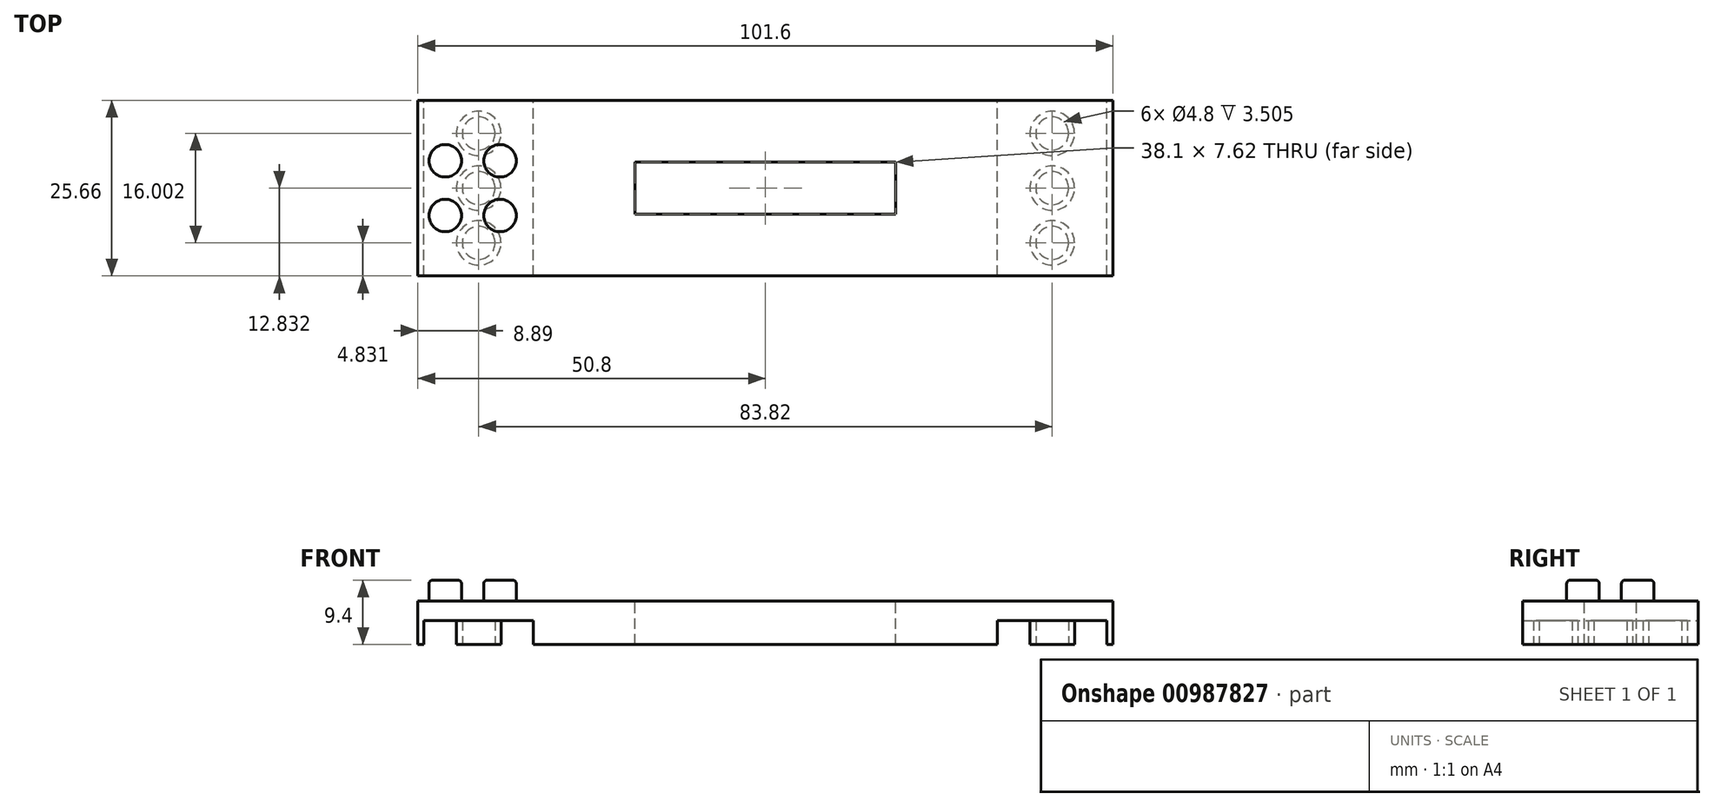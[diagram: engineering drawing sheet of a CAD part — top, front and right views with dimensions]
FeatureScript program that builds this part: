
annotation { "Feature Type Name" : "Feature", "Feature Type Description" : "" }
export const myFeature = defineFeature(function(context is Context, id is Id, definition is map)
    precondition{}
    {
        {
            var Q0;
            Q0=qCreatedBy(makeId("Top.planeOp"),FACE);
            var sketch = newSketch(context, id + "F0", { "sketchPlane" : qUnion([Q0])});
            skLineSegment(sketch, "E0.bottom", {"start": v(0, 0) * mm, "end": v(101.6, 0) * mm});
            skLineSegment(sketch, "E0.top", {"start": v(0, 32) * mm, "end": v(101.6, 32) * mm});
            skLineSegment(sketch, "E0.left", {"start": v(0, 0) * mm, "end": v(0, 32) * mm});
            skLineSegment(sketch, "E0.right", {"start": v(101.6, 0) * mm, "end": v(101.6, 32) * mm});
            skSolve(sketch);
        }
        {
            var Q0;
            Q0=makeQuery(id+"F0.imprint","IMPRINT",FACE,{"disambiguationData":[TD([[makeQuery(id+"F0.imprint","IMPRINT",EDGE,{"derivedFrom":sQuery(id+"F0.wireOp",EDGE,"E0.bottom")}),1.0]])]});
            extrude(context, id + "F1", {"entities" : qUnion([Q0]), "depth" : 6.35 * mm, "offsetDistance" : 25.4 * mm});
        }
        {
            var Q0;
            Q0=makeQuery(id+"F1.opExtrude","CAP_FACE",FACE,{"disambiguationData":[OSD([sQuery(id+"F0.wireOp",EDGE,"E0.bottom"),sQuery(id+"F0.wireOp",EDGE,"E0.top"),sQuery(id+"F0.wireOp",EDGE,"E0.left"),sQuery(id+"F0.wireOp",EDGE,"E0.right")])],"isStart":false});
            var sketch = newSketch(context, id + "F2", { "sketchPlane" : qUnion([Q0])});
            skCircle(sketch, "E1", {"center": v(4, 20) * mm, "radius": 2.37 * mm});
            skCircle(sketch, "E2.0.1.0", {"center": v(4, 12) * mm, "radius": 2.37 * mm});
            skCircle(sketch, "E2.1.0.0", {"center": v(12, 20) * mm, "radius": 2.37 * mm});
            skCircle(sketch, "E2.1.1.0", {"center": v(12, 12) * mm, "radius": 2.37 * mm});
            skLineSegment(sketch, "E2.direction1", {"start": v(4, 20) * mm, "end": v(12, 20) * mm, "construction": true});
            skLineSegment(sketch, "E2.direction2", {"start": v(4, 20) * mm, "end": v(4, 12) * mm, "construction": true});
            skLineSegment(sketch, "E3", {"start": v(4, 20) * mm, "end": v(4, 12) * mm});
            skLineSegment(sketch, "E4", {"start": v(12, 20) * mm, "end": v(12, 12) * mm, "construction": true});
            skLineSegment(sketch, "E5", {"start": v(4, 16) * mm, "end": v(12, 16) * mm, "construction": true});
            skSolve(sketch);
        }
        {
            var Q0;
            Q0=makeQuery(id+"F2.imprint","IMPRINT",FACE,{"disambiguationData":[TD([[makeQuery(id+"F2.imprint","IMPRINT",EDGE,{"derivedFrom":sQuery(id+"F2.wireOp",EDGE,"E2.1.0.0")}),1.0]])]});
            var Q1;
            Q1=makeQuery(id+"F2.imprint","IMPRINT",FACE,{"disambiguationData":[TD([[makeQuery(id+"F2.imprint","IMPRINT",EDGE,{"derivedFrom":sQuery(id+"F2.wireOp",EDGE,"E2.1.1.0")}),1.0]])]});
            var Q2;
            Q2=makeQuery(id+"F2.imprint","IMPRINT",FACE,{"disambiguationData":[TD([[makeQuery(id+"F2.imprint","IMPRINT",EDGE,{"derivedFrom":sQuery(id+"F2.wireOp",EDGE,"E2.0.1.0")}),1.0]])]});
            var Q3;
            Q3=makeQuery(id+"F2.imprint","IMPRINT",FACE,{"disambiguationData":[TD([[makeQuery(id+"F2.imprint","IMPRINT",EDGE,{"derivedFrom":sQuery(id+"F2.wireOp",EDGE,"E1")}),1.0]])]});
            extrude(context, id + "F3", {"entities" : qUnion([Q0, Q1, Q2, Q3]), "operationType" : NewBodyOperationType.ADD, "depth" : 3.05 * mm, "offsetDistance" : 25.4 * mm});
        }
        {
            var Q0;
            Q0=makeQuery(id+"F3.opExtrude","CAP_EDGE",EDGE,{"disambiguationData":[OSD([sQuery(id+"F2.wireOp",EDGE,"E2.1.0.0")])],"isStart":false});
            var Q1;
            Q1=makeQuery(id+"F3.opExtrude","CAP_EDGE",EDGE,{"disambiguationData":[OSD([sQuery(id+"F2.wireOp",EDGE,"E1")])],"isStart":false});
            var Q2;
            Q2=makeQuery(id+"F3.opExtrude","CAP_EDGE",EDGE,{"disambiguationData":[OSD([sQuery(id+"F2.wireOp",EDGE,"E2.0.1.0")])],"isStart":false});
            var Q3;
            Q3=makeQuery(id+"F3.opExtrude","CAP_EDGE",EDGE,{"disambiguationData":[OSD([sQuery(id+"F2.wireOp",EDGE,"E2.1.1.0")])],"isStart":false});
            fillet(context, id + "F4", {"entities" : qUnion([Q0, Q1, Q2, Q3]), "radius" : 0.5 * mm, "tangentPropagation" : true, "allowEdgeOverflow" : false});
        }
        {
            var Q0;
            Q0=makeQuery(id+"F1.opExtrude","CAP_FACE",FACE,{"disambiguationData":[OSD([sQuery(id+"F0.wireOp",EDGE,"E0.bottom"),sQuery(id+"F0.wireOp",EDGE,"E0.top"),sQuery(id+"F0.wireOp",EDGE,"E0.left"),sQuery(id+"F0.wireOp",EDGE,"E0.right")])],"isStart":true});
            var sketch = newSketch(context, id + "F5", { "sketchPlane" : qUnion([Q0])});
            skLineSegment(sketch, "E6.bottom", {"start": v(0, -32) * mm, "end": v(17.78, -32) * mm, "construction": true});
            skLineSegment(sketch, "E6.top", {"start": v(0, 0) * mm, "end": v(17.78, 0) * mm, "construction": true});
            skLineSegment(sketch, "E6.left", {"start": v(0, -32) * mm, "end": v(0, 0) * mm, "construction": true});
            skLineSegment(sketch, "E6.right", {"start": v(17.78, -32) * mm, "end": v(17.78, 0) * mm, "construction": true});
            skLineSegment(sketch, "E7.bottom", {"start": v(101.6, 0) * mm, "end": v(83.82, 0) * mm, "construction": true});
            skLineSegment(sketch, "E7.top", {"start": v(101.6, -32) * mm, "end": v(83.82, -32) * mm, "construction": true});
            skLineSegment(sketch, "E7.left", {"start": v(101.6, 0) * mm, "end": v(101.6, -32) * mm, "construction": true});
            skLineSegment(sketch, "E7.right", {"start": v(83.82, 0) * mm, "end": v(83.82, -32) * mm, "construction": true});
            skCircle(sketch, "E8", {"center": v(8.9, -16) * mm, "radius": 3.25 * mm});
            skCircle(sketch, "E9", {"center": v(8.9, -16) * mm, "radius": 2.4 * mm});
            skCircle(sketch, "E10", {"center": v(8.9, -8) * mm, "radius": 3.25 * mm});
            skCircle(sketch, "E11", {"center": v(8.9, -8) * mm, "radius": 2.4 * mm});
            skCircle(sketch, "E12", {"center": v(8.9, -24) * mm, "radius": 3.25 * mm});
            skCircle(sketch, "E13", {"center": v(8.9, -24) * mm, "radius": 2.4 * mm});
            skCircle(sketch, "E14", {"center": v(92.71, -16) * mm, "radius": 3.25 * mm});
            skCircle(sketch, "E15", {"center": v(92.71, -16) * mm, "radius": 2.4 * mm});
            skCircle(sketch, "E16", {"center": v(92.71, -8) * mm, "radius": 3.25 * mm});
            skCircle(sketch, "E17", {"center": v(92.71, -8) * mm, "radius": 2.4 * mm});
            skCircle(sketch, "E18", {"center": v(92.71, -24) * mm, "radius": 3.25 * mm});
            skCircle(sketch, "E19", {"center": v(92.71, -24) * mm, "radius": 2.4 * mm});
            skLineSegment(sketch, "E20", {"start": v(0, -16) * mm, "end": v(8.9, -16) * mm, "construction": true});
            skLineSegment(sketch, "E21", {"start": v(101.6, -16) * mm, "end": v(92.71, -16) * mm, "construction": true});
            skLineSegment(sketch, "E22", {"start": v(8.9, 0) * mm, "end": v(8.9, -8) * mm, "construction": true});
            skLineSegment(sketch, "E23", {"start": v(92.71, 0) * mm, "end": v(92.71, -8) * mm, "construction": true});
            skLineSegment(sketch, "E24", {"start": v(8.9, -8) * mm, "end": v(8.9, -16) * mm, "construction": true});
            skLineSegment(sketch, "E25", {"start": v(8.9, -16) * mm, "end": v(8.9, -24) * mm, "construction": true});
            skLineSegment(sketch, "E26", {"start": v(92.71, -8) * mm, "end": v(92.71, -16) * mm, "construction": true});
            skLineSegment(sketch, "E27", {"start": v(92.71, -16) * mm, "end": v(92.71, -24) * mm, "construction": true});
            skLineSegment(sketch, "E28.bottom", {"start": v(0.89, -1.5) * mm, "end": v(16.9, -1.5) * mm});
            skLineSegment(sketch, "E28.top", {"start": v(0.89, -30.5) * mm, "end": v(16.9, -30.5) * mm});
            skLineSegment(sketch, "E28.left", {"start": v(0.89, -1.5) * mm, "end": v(0.89, -30.5) * mm});
            skLineSegment(sketch, "E28.right", {"start": v(16.9, -1.5) * mm, "end": v(16.9, -30.5) * mm});
            skLineSegment(sketch, "E29.bottom", {"start": v(84.7, -1.5) * mm, "end": v(100.71, -1.5) * mm});
            skLineSegment(sketch, "E29.top", {"start": v(84.7, -30.5) * mm, "end": v(100.71, -30.5) * mm});
            skLineSegment(sketch, "E29.left", {"start": v(84.7, -1.5) * mm, "end": v(84.7, -30.5) * mm});
            skLineSegment(sketch, "E29.right", {"start": v(100.71, -1.5) * mm, "end": v(100.71, -30.5) * mm});
            skSolve(sketch);
        }
        {
            var Q0;
            Q0=makeQuery(id+"F5.imprint","IMPRINT",FACE,{"disambiguationData":[TD([[makeQuery(id+"F5.imprint","IMPRINT",EDGE,{"derivedFrom":sQuery(id+"F5.wireOp",EDGE,"E8")}),-1.0]])]});
            var Q1;
            Q1=makeQuery(id+"F5.imprint","IMPRINT",FACE,{"disambiguationData":[TD([[makeQuery(id+"F5.imprint","IMPRINT",EDGE,{"derivedFrom":sQuery(id+"F5.wireOp",EDGE,"E14")}),-1.0]])]});
            var Q2;
            Q2=makeQuery(id+"F5.imprint","IMPRINT",FACE,{"disambiguationData":[TD([[makeQuery(id+"F5.imprint","IMPRINT",EDGE,{"derivedFrom":sQuery(id+"F5.wireOp",EDGE,"E11")}),1.0]])]});
            var Q3;
            Q3=makeQuery(id+"F5.imprint","IMPRINT",FACE,{"disambiguationData":[TD([[makeQuery(id+"F5.imprint","IMPRINT",EDGE,{"derivedFrom":sQuery(id+"F5.wireOp",EDGE,"E9")}),1.0]])]});
            var Q4;
            Q4=makeQuery(id+"F5.imprint","IMPRINT",FACE,{"disambiguationData":[TD([[makeQuery(id+"F5.imprint","IMPRINT",EDGE,{"derivedFrom":sQuery(id+"F5.wireOp",EDGE,"E13")}),1.0]])]});
            var Q5;
            Q5=makeQuery(id+"F5.imprint","IMPRINT",FACE,{"disambiguationData":[TD([[makeQuery(id+"F5.imprint","IMPRINT",EDGE,{"derivedFrom":sQuery(id+"F5.wireOp",EDGE,"E17")}),1.0]])]});
            var Q6;
            Q6=makeQuery(id+"F5.imprint","IMPRINT",FACE,{"disambiguationData":[TD([[makeQuery(id+"F5.imprint","IMPRINT",EDGE,{"derivedFrom":sQuery(id+"F5.wireOp",EDGE,"E15")}),1.0]])]});
            var Q7;
            Q7=makeQuery(id+"F5.imprint","IMPRINT",FACE,{"disambiguationData":[TD([[makeQuery(id+"F5.imprint","IMPRINT",EDGE,{"derivedFrom":sQuery(id+"F5.wireOp",EDGE,"E19")}),1.0]])]});
            extrude(context, id + "F6", {"entities" : qUnion([Q0, Q1, Q2, Q3, Q4, Q5, Q6, Q7]), "operationType" : NewBodyOperationType.REMOVE, "oppositeDirection" : true, "depth" : 3.5 * mm, "offsetDistance" : 25.4 * mm});
        }
        {
            var Q0;
            {var subQ0=sQuery(id+"F0.wireOp",EDGE,"E0.bottom");var subQ1=sQuery(id+"F0.wireOp",EDGE,"E0.right");var subQ2=sQuery(id+"F0.wireOp",EDGE,"E0.top");var subQ3=sQuery(id+"F0.wireOp",EDGE,"E0.left");Q0=makeQuery(id+"F6.boolean.opBoolean","SPLIT",FACE,{"disambiguationData":[TD([makeQuery(id+"F1.opExtrude","SWEPT_FACE",FACE,{"disambiguationData":[OSD([subQ0])]})])],"derivedFrom":makeQuery(id+"F1.opExtrude","CAP_FACE",FACE,{"disambiguationData":[OSD([subQ0,subQ2,subQ3,subQ1])],"isStart":true})});}
            var sketch = newSketch(context, id + "F7", { "sketchPlane" : qUnion([Q0])});
            skLineSegment(sketch, "E30.bottom", {"start": v(101.6, -32) * mm, "end": v(0, -32) * mm});
            skLineSegment(sketch, "E30.top", {"start": v(101.6, -28.83) * mm, "end": v(0, -28.83) * mm});
            skLineSegment(sketch, "E30.left", {"start": v(101.6, -32) * mm, "end": v(101.6, -28.83) * mm});
            skLineSegment(sketch, "E30.right", {"start": v(0, -32) * mm, "end": v(0, -28.83) * mm});
            skLineSegment(sketch, "E31.bottom", {"start": v(101.6, 0) * mm, "end": v(0, 0) * mm});
            skLineSegment(sketch, "E31.top", {"start": v(101.6, -3.17) * mm, "end": v(0, -3.18) * mm});
            skLineSegment(sketch, "E31.left", {"start": v(101.6, 0) * mm, "end": v(101.6, -3.17) * mm});
            skLineSegment(sketch, "E31.right", {"start": v(0, 0) * mm, "end": v(0, -3.18) * mm});
            skSolve(sketch);
        }
        {
            var Q0;
            Q0 = qSketchRegion(id + "F7", true);
            extrude(context, id + "F8", {"entities" : qUnion([Q0]), "operationType" : NewBodyOperationType.REMOVE, "endBound" : BoundingType.UP_TO_NEXT, "oppositeDirection" : true, "depth" : 25.4 * mm, "offsetDistance" : 25.4 * mm});
        }
        {
            var Q0;
            Q0=makeQuery(id+"F1.opExtrude","CAP_FACE",FACE,{"disambiguationData":[OSD([sQuery(id+"F0.wireOp",EDGE,"E0.bottom"),sQuery(id+"F0.wireOp",EDGE,"E0.top"),sQuery(id+"F0.wireOp",EDGE,"E0.left"),sQuery(id+"F0.wireOp",EDGE,"E0.right")])],"isStart":false});
            var sketch = newSketch(context, id + "F9", { "sketchPlane" : qUnion([Q0])});
            skLineSegment(sketch, "E32.bottom", {"start": v(69.85, 12.2) * mm, "end": v(31.75, 12.2) * mm});
            skLineSegment(sketch, "E32.top", {"start": v(69.85, 19.81) * mm, "end": v(31.75, 19.81) * mm});
            skLineSegment(sketch, "E32.left", {"start": v(69.85, 12.2) * mm, "end": v(69.85, 19.81) * mm});
            skLineSegment(sketch, "E32.right", {"start": v(31.75, 12.2) * mm, "end": v(31.75, 19.81) * mm});
            skLineSegment(sketch, "E33", {"start": v(69.85, 16) * mm, "end": v(101.6, 16) * mm, "construction": true});
            skLineSegment(sketch, "E34", {"start": v(50.8, 12.2) * mm, "end": v(50.8, 3.18) * mm, "construction": true});
            skSolve(sketch);
        }
        {
            var Q0;
            Q0 = qSketchRegion(id + "F9", true);
            extrude(context, id + "F10", {"entities" : qUnion([Q0]), "operationType" : NewBodyOperationType.REMOVE, "endBound" : BoundingType.UP_TO_NEXT, "oppositeDirection" : true, "depth" : 25.4 * mm, "offsetDistance" : 25.4 * mm});
        }
    });
